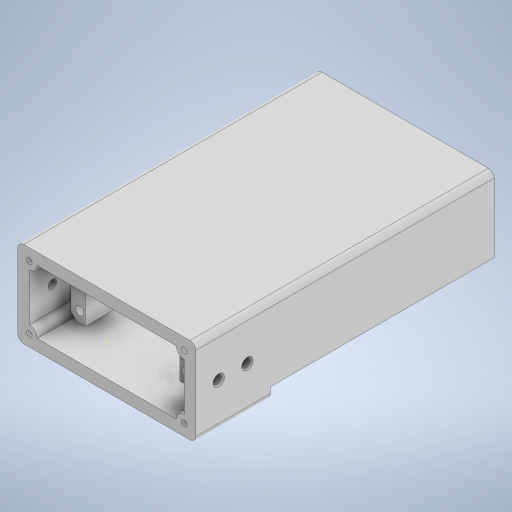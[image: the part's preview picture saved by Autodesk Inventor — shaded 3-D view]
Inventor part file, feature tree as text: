
AUTODESK INVENTOR PART (.ipt)
format: ipt  version: 2023.1 (Build 271208000, 208)  size: 495,616 bytes
history: native  units: mm
features: extrude x15, sketch x12, fillet x3, chamfer x3, projected_geometry x2, other x1, mirror x1
ambient origin geometry x8: Origin, YZ Plane, XZ Plane, XY Plane, X Axis, Y Axis, Z Axis, Center Point
bodies: Body1 (feature_tree)
feature tree (37):
  other  "솔리드1"
  sketch  "스케치1"
  extrude  "돌출1"  Depth=54.0mm
  extrude  "돌출2"  Depth=22.0mm
  sketch  "스케치2"
  extrude  "돌출3"  Depth=20.0mm
  fillet  "모깎기1"  Radius=10.0mm
  extrude  "돌출4"  Depth=30.0mm
  sketch  "스케치3"
  extrude  "돌출5"  Depth=11.0mm
  extrude  "돌출6"  Depth=1.0mm
  chamfer  "모따기1"  Distance=4.0mm
  extrude  "돌출7"  Depth=3.0mm TaperAngle=0.0deg
  extrude  "돌출8"  Depth=75.0mm TaperAngle=0.0deg
  sketch  "스케치6"
  extrude  "돌출9"  Depth=1.0mm
  extrude  "돌출10"  Depth=8.726646mm
  extrude  "돌출11"  Depth=74.0mm TaperAngle=0.0deg
  chamfer  "모따기2"  Distance=0.5mm
  fillet  "모깎기2"  Radius=3.0mm
  extrude  "돌출12"  Depth=25.1mm
  extrude  "돌출13"  Depth=52.1mm
  extrude  "돌출14"  Depth=31.2mm
  fillet  "모깎기4"  Radius=57.6mm
  sketch  "스케치13"
  extrude  "돌출15"  Depth=3.0mm
  mirror  "미러1"
  chamfer  "모따기4"  Distance=5.0mm
  sketch  "스케치4"
  sketch  "스케치5"
  projected_geometry  "투영된 루프1"
  sketch  "스케치7"
  sketch  "스케치8"
  projected_geometry  "투영된 루프2"
  sketch  "스케치9"
  sketch  "스케치10"
  sketch  "스케치14"
